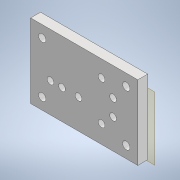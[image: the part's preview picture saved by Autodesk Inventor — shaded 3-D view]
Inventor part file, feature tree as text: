
AUTODESK INVENTOR PART (.ipt)
format: ipt  version: 2021 (Build 250183000, 183)  size: 173,568 bytes
history: native  units: in
note: dims shown in document units (in); Inventor stores cm internally (conversion verified against a paired STEP export)
features: reference x16, other x9, extrude x3, hole x3, sketch x3, plane x1, projected_geometry x1
ambient origin geometry x8: Origin, YZ Plane, XZ Plane, XY Plane, X Axis, Y Axis, Z Axis, Center Point
bodies: Solid1 (feature_tree)
feature tree (36):
  extrude  "Extrusion base plate"  [1 undecoded]
  plane  "work plane for rib creation"
  other  "channels as rib"
  extrude  "extrusion of ribs to get cutout"  Depth=0.2756in
  extrude  "valve space extrusion"  Depth=0.2362in TaperAngle=0.0deg
  other  "projected points for every valve"
  other  "all valve spaces"
  hole  "holes for control layer"  [1 undecoded]
  hole  "holes for connection to flow layer"  [1 undecoded]
  hole  "holes in corners"  [1 undecoded]
  sketch  "Sketch1"  dims[d0=0.2362in d1=0.0in d2=-0.0394in]
  reference  "Reference1"
  reference  "Reference2"
  reference  "Reference3"
  reference  "Reference4"
  other  "channels and points for valves and for connectors for control layer"
  reference  "Reference5"
  reference  "Reference6"
  reference  "Reference7"
  reference  "Reference8"
  reference  "Reference9"
  reference  "Reference10"
  reference  "Reference11"
  sketch  "Sketch3"  dims[d3=0.2756in d4=0.2756in]
  projected_geometry  "Projected Loop1"
  sketch  "Sketch4"  dims[d11=0.0394in d12=0.0394in d13=0.0in d14=0.0in d15=0.0394in d16=0.0in d17=0.1024in d18=0.0in d19=0.1181in d20=0.0886in d21=0.063in d22=0.0in d23=0.1614in d24=0.2362in d25=0.1575in d26=0.0787in d27=90.0deg d28=0.0394in d29=0.0in d30=0.1614in d31=0.2362in d32=0.1575in d33=0.0787in d34=90.0deg d35=0.2106in d36=0.0in d37=0.1772in d38=0.2362in d39=0.1575in d40=0.0787in d41=90.0deg d42=0.4144in d43=0.0in]
  reference  "Reference12"
  other  "projected points for every hole for control layer only"
  other  "projected points for every hole for flow layer only"
  other  "prohected points for corner holes"
  reference  "Reference13"
  reference  "Reference14"
  reference  "Reference15"
  reference  "Reference16"
  other  "Prototype Assembly.iam"
  other  "Prototype Flow Layer:1"
note: 4 required parameter values undecoded (feature->parameter linkage not recoverable at this tier; creation-order binding heuristic only, values carry confidence <= 0.55)
